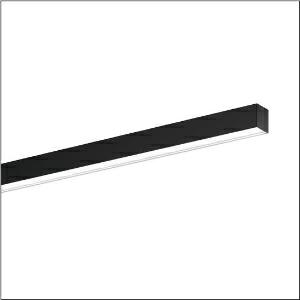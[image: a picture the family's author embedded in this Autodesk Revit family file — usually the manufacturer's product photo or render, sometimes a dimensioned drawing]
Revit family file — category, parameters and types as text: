
# Revit family: silica_r__21_51mx23db35bb_4e5d
name_source: partatom
category: Lighting Fixtures
units: mm (PartAtom-declared; Revit-internal decimal feet)

## family parameters
Cut with Voids When Loaded = No
Host = Face
Light Source = No
Part Type = Normal
Room Calculation Point = No
Round Connector Dimension = Use Diameter
Shared = No

## types (1)
- --- (1 x LED, 4100 lm, 30.1 W, 3000K)
    Apparent Load = 30 VA
    CIE Flux Codes = 78 96 99 100 100
    Color Rendering = 80
    Color Temperature = 3000K
    Default Elevation = 1800 mm
    Description = Silica® 21, office luminaire, primary optical cover: prismatic diffuser, of PMMA, CAT 2 (L<= 3000cd/m²), light emission: direct distribution, primary light characteristic: symmetric, installation type: surface-mounted, LED, rated luminous flux: 4.100lm, luminous efficacy: 136lm/W, light colour: 830, colour temperature: 3000K, with terminal, 3+2-pole, max. 2.5mm², mains connection: 220..240V, AC, 50/60Hz, rated input power: 30.1W, luminaire housing, of aluminium, jet black (RAL 9005), length: 1.504mm, width: 53mm, height: 53mm, protection rating (complete): IP20, insulation class (complete): insulation class I (protective earthing), certification: CE, permissible operating ambient temperature: 0..+35°C, standard: EN 50419, packaging unit: 1 piece
    Height = 0 mm  [stored 0 ft]
    Lamp = 1 x LED
    Lamp Light Flux = 4100 lm
    Lamp Power = 30.1 W
    Lamp count = 1
    Length = 1504 mm
    Luminous efficacy = 136 lm/W
    Manufacturer = Siteco
    ModVariant = No
    Model = 51MX23DB35BB
    Mounting Place = Ceiling
    Mounting Type = Recessed
    Number of Poles = 1
    OnlyDefault = Yes
    Power Factor = 1
    Product Name = Silica® 21
    Product group = office luminaire | ceiling recessed
    ProductGroupID = 401
    Protection Class = Protection class I
    Protection Degree = IP 20
    RLX_Detail_Level = 1
    RLX_Emergency_Light_Flux = 0 lm
    RLX_Emergency_Type = 0
    RLX_Emergency_Type_DB = No
    RlxData = <blob elided: 23661 chars, md5=ee4ae70e>
    Socket = socket
    Standby Power = 0 W
    System Light Flux = 4100 lm
    System Power = 30 W
    Type Comments = factory setting: luminous flux: 100 % | dim-lin: 254 | 345 mA
    Type Image = l_1313584.jpg
    URL = http://relux.com
    VarID = @adj_068065
    Voltage = 0 V
    Weight = 0.00 kg
    Width = 53 mm

note: [stored X ft] marks values corroborated as IEEE doubles in the binary element streams (Revit-internal decimal feet)

## geometry (parser evidence)
native form markers: Blend x4, Sweep x10
no freeform markers — native parametric forms only
